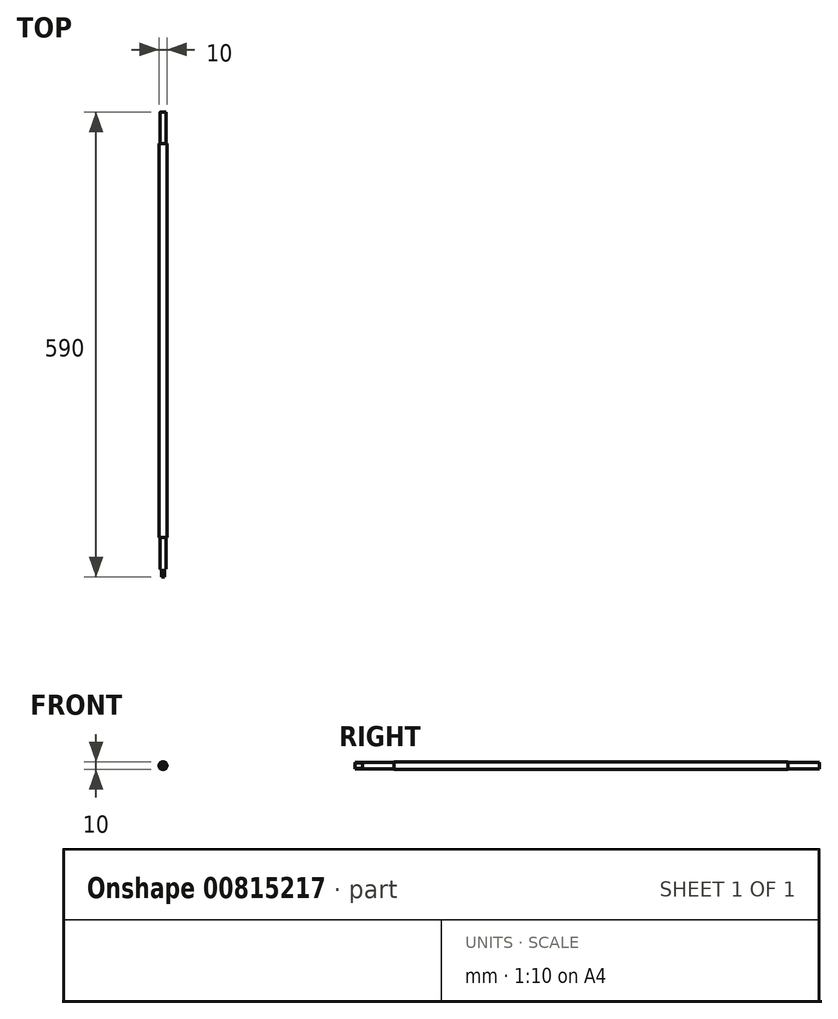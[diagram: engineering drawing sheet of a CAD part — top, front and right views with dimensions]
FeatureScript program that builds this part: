
annotation { "Feature Type Name" : "Feature", "Feature Type Description" : "" }
export const myFeature = defineFeature(function(context is Context, id is Id, definition is map)
    precondition{}
    {
        {
            var Q0;
            Q0=qCreatedBy(makeId("Front.planeOp"),FACE);
            var sketch = newSketch(context, id + "F0", { "sketchPlane" : qUnion([Q0])});
            skCircle(sketch, "E0", {"center": v(0, 0) * mm, "radius": 5 * mm});
            skSolve(sketch);
        }
        {
            var Q0;
            Q0=qSketchRegion(id+"F0",true);
            extrude(context, id + "F1", {"entities" : qUnion([Q0]), "endBound" : BoundingType.SYMMETRIC, "oppositeDirection" : true, "depth" : (500 + 50 + 40) * mm, "offsetDistance" : 25 * mm});
        }
        {
            var Q0;
            Q0=makeQuery(id+"F1.opExtrude","CAP_FACE",FACE,{"disambiguationData":[OSD([sQuery(id+"F0.wireOp",EDGE,"E0")])],"isStart":true});
            var sketch = newSketch(context, id + "F2", { "sketchPlane" : qUnion([Q0])});
            skCircle(sketch, "E1", {"center": v(0, 0) * mm, "radius": 4 * mm});
            skCircle(sketch, "E2.0", {"center": v(0, 0) * mm, "radius": 9 * mm});
            skSolve(sketch);
        }
        {
            var Q0;
            Q0=qSketchRegion(id+"F2",true);
            extrude(context, id + "F3", {"entities" : qUnion([Q0]), "operationType" : NewBodyOperationType.REMOVE, "oppositeDirection" : true, "depth" : 50 * mm, "offsetDistance" : 25 * mm});
        }
        {
            var Q0;
            Q0=makeQuery(id+"F1.opExtrude","CAP_FACE",FACE,{"disambiguationData":[OSD([sQuery(id+"F0.wireOp",EDGE,"E0")])],"isStart":false});
            var sketch = newSketch(context, id + "F4", { "sketchPlane" : qUnion([Q0])});
            skCircle(sketch, "E3.0", {"center": v(0, 0) * mm, "radius": 5 * mm});
            skCircle(sketch, "E4", {"center": v(0, 0) * mm, "radius": 4 * mm});
            skSolve(sketch);
        }
        {
            var Q0;
            Q0=qSketchRegion(id+"F4",true);
            extrude(context, id + "F5", {"entities" : qUnion([Q0]), "operationType" : NewBodyOperationType.REMOVE, "oppositeDirection" : true, "depth" : 40 * mm, "offsetDistance" : 25 * mm});
        }
        {
            var Q0;
            Q0=makeQuery(id+"F1.opExtrude","CAP_FACE",FACE,{"disambiguationData":[OSD([sQuery(id+"F0.wireOp",EDGE,"E0")])],"isStart":true});
            var sketch = newSketch(context, id + "F6", { "sketchPlane" : qUnion([Q0])});
            skLineSegment(sketch, "E5.bottom", {"start": v(2, -9.21) * mm, "end": v(-2, -9.21) * mm});
            skLineSegment(sketch, "E5.left", {"start": v(2, -9.21) * mm, "end": v(2, 9.21) * mm});
            skLineSegment(sketch, "E5.right", {"start": v(-2, -9.21) * mm, "end": v(-2, 9.21) * mm});
            skPoint(sketch, "E5.middle", {"position": v(0, 0) * mm});
            skLineSegment(sketch, "E6", {"start": v(2, 9.21) * mm, "end": v(8.24, 9.21) * mm});
            skLineSegment(sketch, "E7", {"start": v(8.24, 9.21) * mm, "end": v(8.24, -15.57) * mm});
            skLineSegment(sketch, "E8", {"start": v(8.24, -15.57) * mm, "end": v(-11.6, -12.26) * mm});
            skLineSegment(sketch, "E9", {"start": v(-11.6, -12.26) * mm, "end": v(-11.6, 9.21) * mm});
            skLineSegment(sketch, "E10", {"start": v(-11.6, 9.21) * mm, "end": v(-2, 9.21) * mm});
            skSolve(sketch);
        }
        {
            var Q0;
            Q0 = qSketchRegion(id + "F6", true);
            extrude(context, id + "F7", {"entities" : qUnion([Q0]), "operationType" : NewBodyOperationType.REMOVE, "oppositeDirection" : true, "depth" : 10 * mm, "offsetDistance" : 25 * mm});
        }
    });
